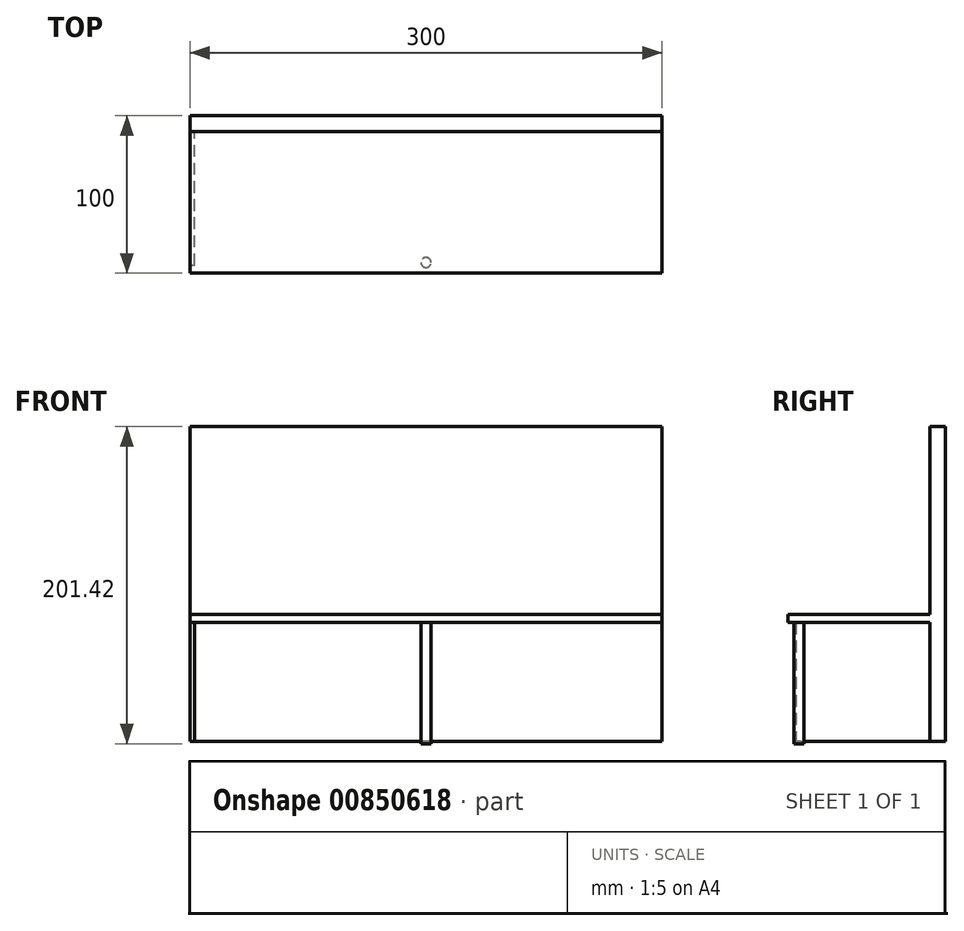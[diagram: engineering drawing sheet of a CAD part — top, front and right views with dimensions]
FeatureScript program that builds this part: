
annotation { "Feature Type Name" : "Feature", "Feature Type Description" : "" }
export const myFeature = defineFeature(function(context is Context, id is Id, definition is map)
    precondition{}
    {
        {
            var Q0;
            Q0=qCreatedBy(makeId("Top.planeOp"),FACE);
            var sketch = newSketch(context, id + "F0", { "sketchPlane" : qUnion([Q0])});
            skLineSegment(sketch, "E0.bottom", {"start": v(150, 20.7) * mm, "end": v(-150, 20.7) * mm});
            skLineSegment(sketch, "E0.top", {"start": v(150, 10.7) * mm, "end": v(-150, 10.7) * mm});
            skLineSegment(sketch, "E0.left", {"start": v(150, 20.7) * mm, "end": v(150, 10.7) * mm});
            skLineSegment(sketch, "E0.right", {"start": v(-150, 20.7) * mm, "end": v(-150, 10.7) * mm});
            skPoint(sketch, "E0.middle", {"position": v(0, 15.7) * mm});
            skSolve(sketch);
        }
        {
            var Q0;
            Q0 = qSketchRegion(id + "F0", true);
            extrude(context, id + "F1", {"entities" : qUnion([Q0]), "depth" : 200 * mm, "offsetDistance" : 25 * mm});
        }
        {
            var Q0;
            Q0=makeQuery(id+"F1.opExtrude","SWEPT_FACE",FACE,{"disambiguationData":[OSD([sQuery(id+"F0.wireOp",EDGE,"E0.top")])]});
            var sketch = newSketch(context, id + "F2", { "sketchPlane" : qUnion([Q0])});
            skLineSegment(sketch, "E1.bottom", {"start": v(-150, 80.58) * mm, "end": v(150, 80.58) * mm});
            skLineSegment(sketch, "E1.top", {"start": v(-150, 75.58) * mm, "end": v(150, 75.58) * mm});
            skLineSegment(sketch, "E1.left", {"start": v(-150, 80.58) * mm, "end": v(-150, 75.58) * mm});
            skLineSegment(sketch, "E1.right", {"start": v(150, 80.58) * mm, "end": v(150, 75.58) * mm});
            skSolve(sketch);
        }
        {
            var Q0;
            Q0 = qSketchRegion(id + "F2", true);
            extrude(context, id + "F3", {"entities" : qUnion([Q0]), "operationType" : NewBodyOperationType.ADD, "depth" : 90 * mm, "offsetDistance" : 25 * mm});
        }
        {
            var Q0;
            {var subQ2=sQuery(id+"F0.wireOp",EDGE,"E0.top");Q0=makeQuery(id+"F3.boolean.opBoolean","SPLIT",FACE,{"disambiguationData":[TD([makeQuery(id+"F3.opExtrude","SWEPT_FACE",FACE,{"disambiguationData":[OSD([sQuery(id+"F2.wireOp",EDGE,"E1.top")])]})])],"derivedFrom":makeQuery(id+"F1.opExtrude","SWEPT_FACE",FACE,{"disambiguationData":[OSD([subQ2])]})});}
            var sketch = newSketch(context, id + "F4", { "sketchPlane" : qUnion([Q0])});
            skLineSegment(sketch, "E2.bottom", {"start": v(-150, 75.58) * mm, "end": v(-147, 75.58) * mm});
            skLineSegment(sketch, "E2.top", {"start": v(-150, 0) * mm, "end": v(-147, 0) * mm});
            skLineSegment(sketch, "E2.left", {"start": v(-150, 75.58) * mm, "end": v(-150, 0) * mm});
            skLineSegment(sketch, "E2.right", {"start": v(-147, 75.58) * mm, "end": v(-147, 0) * mm});
            skSolve(sketch);
        }
        {
            var Q0;
            Q0 = qSketchRegion(id + "F4", true);
            extrude(context, id + "F5", {"entities" : qUnion([Q0]), "operationType" : NewBodyOperationType.ADD, "depth" : 85 * mm, "offsetDistance" : 25 * mm});
        }
        {
            var Q0;
            Q0=makeQuery(id+"F3.opExtrude","SWEPT_FACE",FACE,{"disambiguationData":[OSD([sQuery(id+"F2.wireOp",EDGE,"E1.top")])]});
            var sketch = newSketch(context, id + "F6", { "sketchPlane" : qUnion([Q0])});
            skCircle(sketch, "E3", {"center": v(0, 72.5) * mm, "radius": 3.19 * mm});
            skSolve(sketch);
        }
        {
            var Q0;
            Q0 = qSketchRegion(id + "F6", true);
            extrude(context, id + "F7", {"entities" : qUnion([Q0]), "operationType" : NewBodyOperationType.ADD, "depth" : 77 * mm, "offsetDistance" : 25 * mm});
        }
    });
